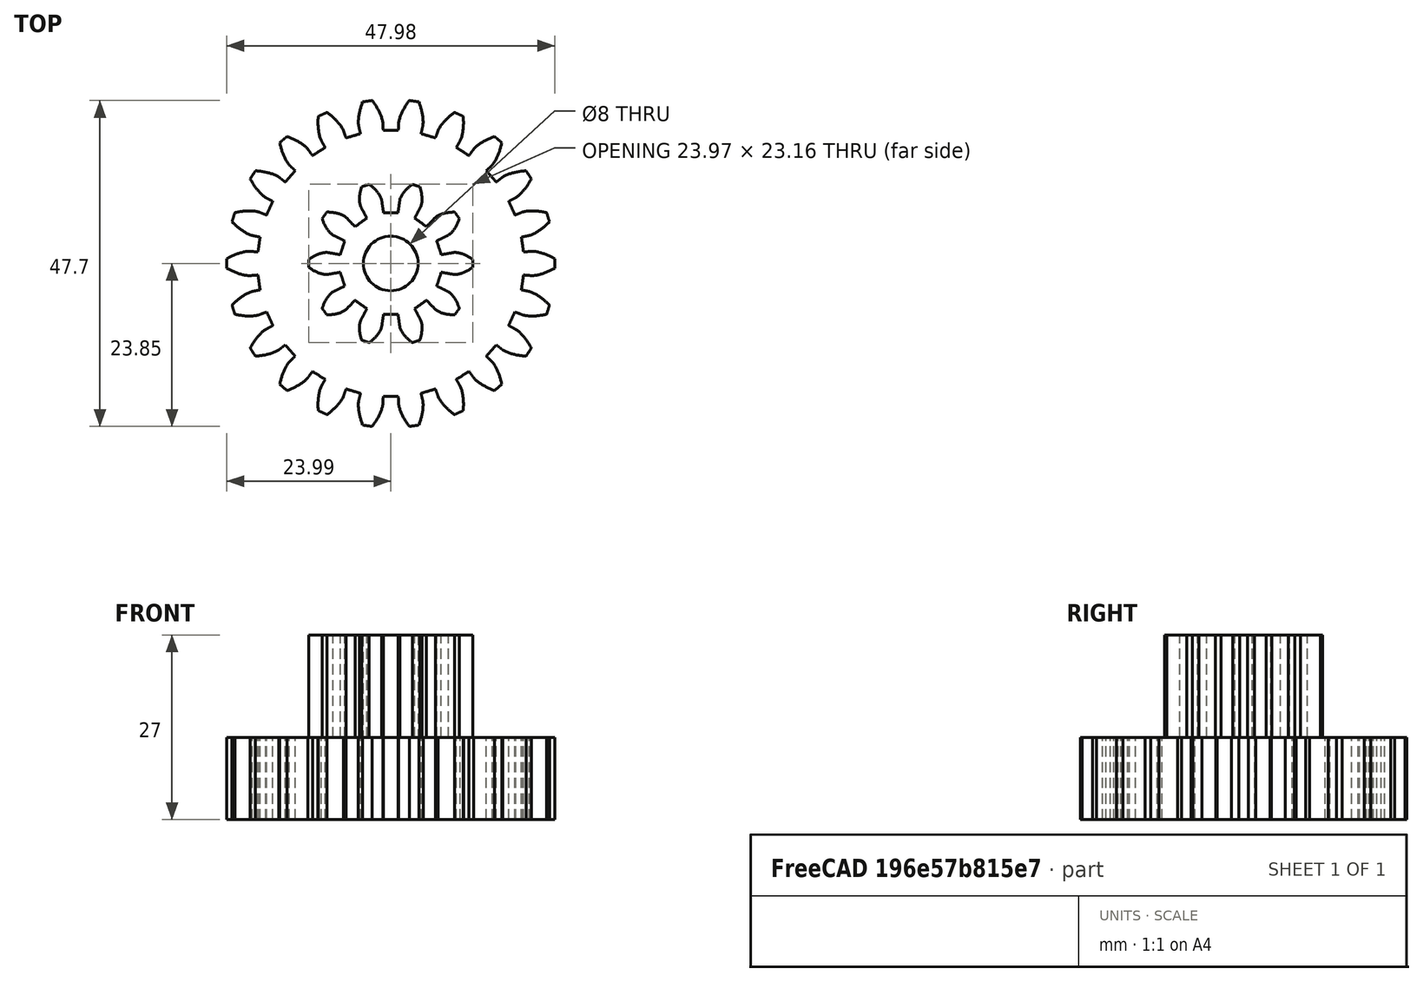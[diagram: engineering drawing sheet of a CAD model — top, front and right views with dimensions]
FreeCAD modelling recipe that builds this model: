
FCSTD DOCUMENT  (FreeCAD 0.17R13522 (Git))
Label: GearboxGear2
License: All rights reserved
LicenseURL: http://en.wikipedia.org/wiki/All_rights_reserved
objects: Part::FeaturePython×2, Part::MultiFuse×1, Sketcher::SketchObject×1, PartDesign::Pocket×1, PartDesign::Body×1, App::Part×1
note: 7 computed .brp shape members not serialized (recipe doc carries the construction recipe); baked Part::Feature solids carry a one-line shape summary decoded from their .brp

FEATURE [Part::FeaturePython] InvoluteGear002  # WARN: FeaturePython — macro-defined, semantics opaque (R4)
  backlash = 0
  beta = 0
  clearance = 0.25
  double_helix = false
  head = 0
  height = 12
  module = 2
  numpoints = 6
  pressure_angle = 20
  reversed_backlash = false
  shift = 0
  simple = false
  teeth = 22
  undercut = false
FEATURE [Part::FeaturePython] InvoluteGear003  # WARN: FeaturePython — macro-defined, semantics opaque (R4)
  Placement = pos=(0,0,12) rot=(0,0,1;0rad)
  backlash = 0
  beta = 0
  clearance = 0.25
  double_helix = false
  head = 0
  height = 15
  module = 2
  numpoints = 6
  pressure_angle = 20
  reversed_backlash = false
  shift = 0
  simple = false
  teeth = 10
  undercut = false
FEATURE [Part::MultiFuse] Fusion001  label="Fusion"
  Shapes = -> [InvoluteGear002,InvoluteGear003]
FEATURE [Sketcher::SketchObject] Sketch
  MapMode = 5
  Placement = pos=(0,0,27) rot=(0,0,1;0rad)
  Support = -> [Fusion001]
  sketch-geometry (1):
    g0: Circle CenterX=0 CenterY=0 CenterZ=0 NormalX=0 NormalY=0 NormalZ=1 AngleXU=0 Radius=4
  constraints (2):
    c: Coincident(g0,g-1)
    c: Radius(g0) = 4
FEATURE [PartDesign::Pocket] Pocket
  Length = 27
  Length2 = 100
  Profile = -> Sketch
  Type = 0
FEATURE [PartDesign::Body] Body001  label="Body"
  Group = -> [Sketch,Pocket]
  Origin = -> Origin003
  Tip = -> Pocket
FEATURE [App::Part] Part001  label="Part"
  Group = -> [Body001,InvoluteGear002,InvoluteGear003,Fusion001]
  License = CC BY 3.0
  LicenseURL = http://creativecommons.org/licenses/by/3.0/
  Origin = -> Origin002
